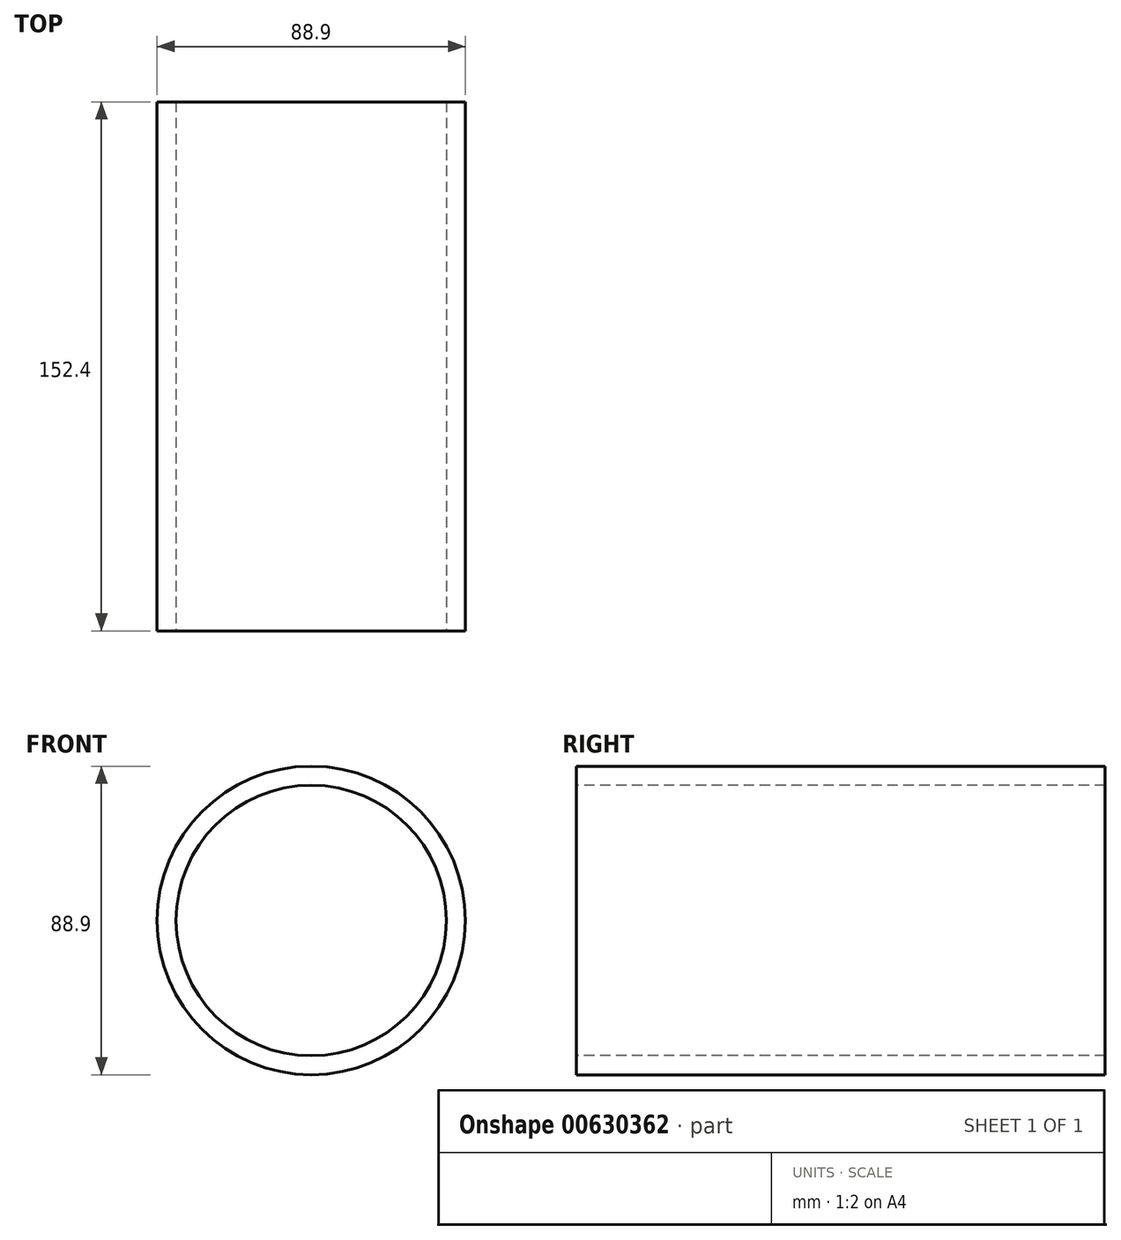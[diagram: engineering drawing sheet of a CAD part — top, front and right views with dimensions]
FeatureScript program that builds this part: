
annotation { "Feature Type Name" : "Feature", "Feature Type Description" : "" }
export const myFeature = defineFeature(function(context is Context, id is Id, definition is map)
    precondition{}
    {
        {
            var Q0;
            Q0=qCreatedBy(makeId("Front.planeOp"),FACE);
            var sketch = newSketch(context, id + "F0", { "sketchPlane" : qUnion([Q0])});
            skCircle(sketch, "E0", {"center": v(0, 0) * mm, "radius": 44.45 * mm});
            skCircle(sketch, "E1", {"center": v(0, 0) * mm, "radius": 38.96 * mm});
            skSolve(sketch);
        }
        {
            var Q0;
            Q0 = qSketchRegion(id + "F0", true);
            extrude(context, id + "F1", {"entities" : qUnion([Q0]), "oppositeDirection" : true, "depth" : 152.4 * mm, "offsetDistance" : 25.4 * mm});
        }
    });
